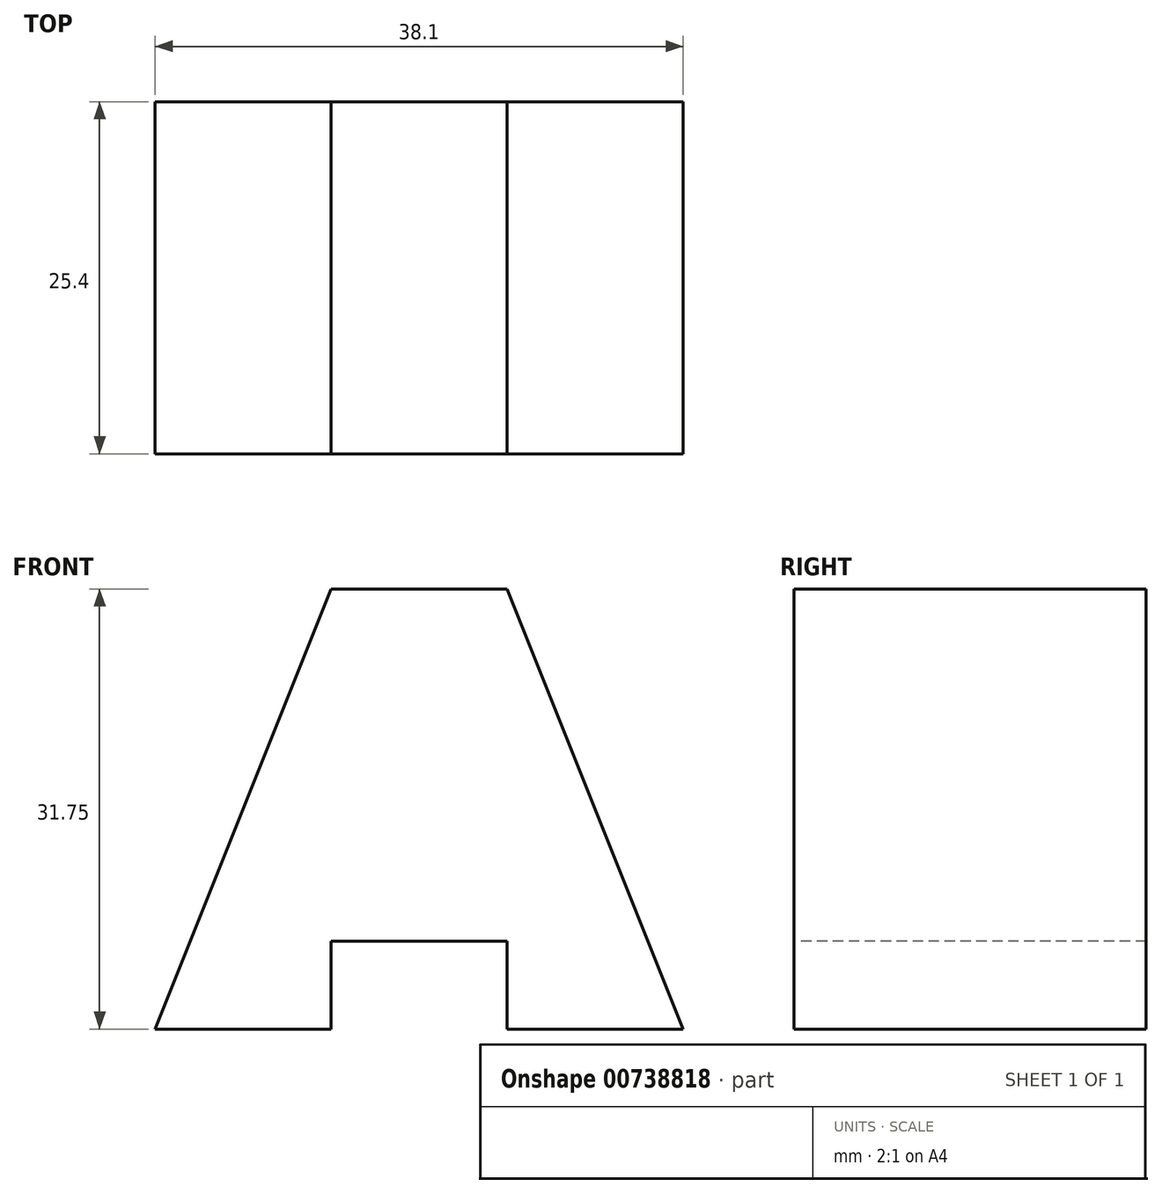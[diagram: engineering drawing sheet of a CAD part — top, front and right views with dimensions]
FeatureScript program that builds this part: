
annotation { "Feature Type Name" : "Feature", "Feature Type Description" : "" }
export const myFeature = defineFeature(function(context is Context, id is Id, definition is map)
    precondition{}
    {
        {
            var Q0;
            Q0=qCreatedBy(makeId("Front.planeOp"),FACE);
            var sketch = newSketch(context, id + "F0", { "sketchPlane" : qUnion([Q0])});
            skLineSegment(sketch, "E0", {"start": v(0, 0) * mm, "end": v(0, 31.75) * mm});
            skLineSegment(sketch, "E1", {"start": v(0, 31.75) * mm, "end": v(38.1, 31.75) * mm});
            skLineSegment(sketch, "E2", {"start": v(38.1, 31.75) * mm, "end": v(38.1, 0) * mm});
            skLineSegment(sketch, "E3", {"start": v(38.1, 0) * mm, "end": v(0, 0) * mm});
            skSolve(sketch);
        }
        {
            var Q0;
            Q0 = qSketchRegion(id + "F0", true);
            extrude(context, id + "F1", {"entities" : qUnion([Q0]), "depth" : 25.4 * mm, "offsetDistance" : 25.4 * mm});
        }
        {
            var Q0;
            Q0=makeQuery(id+"F1.opExtrude","CAP_FACE",FACE,{"disambiguationData":[OSD([sQuery(id+"F0.wireOp",EDGE,"E0"),sQuery(id+"F0.wireOp",EDGE,"E1"),sQuery(id+"F0.wireOp",EDGE,"E2"),sQuery(id+"F0.wireOp",EDGE,"E3")])],"isStart":false});
            var sketch = newSketch(context, id + "F2", { "sketchPlane" : qUnion([Q0])});
            skLineSegment(sketch, "E4", {"start": v(12.7, 0) * mm, "end": v(12.7, 6.35) * mm});
            skLineSegment(sketch, "E5", {"start": v(25.4, 6.35) * mm, "end": v(12.7, 6.35) * mm});
            skLineSegment(sketch, "E6", {"start": v(25.4, 6.35) * mm, "end": v(25.4, 0) * mm});
            skLineSegment(sketch, "E7", {"start": v(25.4, 0) * mm, "end": v(38.1, 0) * mm});
            skSolve(sketch);
        }
        {
            var Q0;
            {var subQ0=sQuery(id+"F2.wireOp",EDGE,"E4");Q0=makeQuery(id+"F2.imprint","IMPRINT",FACE,{"disambiguationData":[TD([[makeQuery(id+"F2.imprint","IMPRINT",EDGE,{"derivedFrom":subQ0}),-1.0]])]});}
            extrude(context, id + "F3", {"entities" : qUnion([Q0]), "operationType" : NewBodyOperationType.REMOVE, "endBound" : BoundingType.THROUGH_ALL, "oppositeDirection" : true, "depth" : 25.4 * mm, "offsetDistance" : 25.4 * mm});
        }
        {
            var Q0;
            Q0=makeQuery(id+"F1.opExtrude","CAP_FACE",FACE,{"disambiguationData":[OSD([sQuery(id+"F0.wireOp",EDGE,"E0"),sQuery(id+"F0.wireOp",EDGE,"E1"),sQuery(id+"F0.wireOp",EDGE,"E2"),sQuery(id+"F0.wireOp",EDGE,"E3")])],"isStart":false});
            var sketch = newSketch(context, id + "F4", { "sketchPlane" : qUnion([Q0])});
            skLineSegment(sketch, "E8", {"start": v(0, 0) * mm, "end": v(12.7, 31.75) * mm});
            skLineSegment(sketch, "E9", {"start": v(12.7, 31.75) * mm, "end": v(25.4, 31.75) * mm});
            skLineSegment(sketch, "E10", {"start": v(25.4, 31.75) * mm, "end": v(38.1, 0) * mm});
            skLineSegment(sketch, "E11", {"start": v(0, 31.75) * mm, "end": v(12.7, 31.75) * mm});
            skLineSegment(sketch, "E12", {"start": v(25.4, 31.75) * mm, "end": v(38.1, 31.75) * mm});
            skSolve(sketch);
        }
        {
            var Q0;
            Q0=makeQuery(id+"F4.imprint","IMPRINT",FACE,{"disambiguationData":[TD([[makeQuery(id+"F4.imprint","IMPRINT",EDGE,{"derivedFrom":sQuery(id+"F4.wireOp",EDGE,"E8")}),1.0]])]});
            var Q1;
            Q1=makeQuery(id+"F4.imprint","IMPRINT",FACE,{"disambiguationData":[TD([[makeQuery(id+"F4.imprint","IMPRINT",EDGE,{"derivedFrom":sQuery(id+"F4.wireOp",EDGE,"E10")}),1.0]])]});
            extrude(context, id + "F5", {"entities" : qUnion([Q0, Q1]), "operationType" : NewBodyOperationType.REMOVE, "endBound" : BoundingType.THROUGH_ALL, "oppositeDirection" : true, "depth" : 25.4 * mm, "offsetDistance" : 25.4 * mm});
        }
    });
